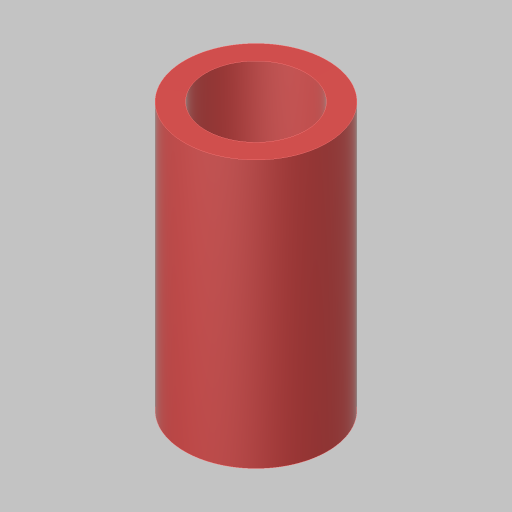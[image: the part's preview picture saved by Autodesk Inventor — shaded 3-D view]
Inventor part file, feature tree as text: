
AUTODESK INVENTOR PART (.ipt)
format: ipt  version: 2023.5 (Build 275446000, 446)  size: 101,888 bytes
history: native  units: in
note: dims shown in document units (in); Inventor stores cm internally (conversion verified against a paired STEP export)
features: extrude x1, sketch x1
ambient origin geometry x8: Origin, YZ Plane, XZ Plane, XY Plane, X Axis, Y Axis, Z Axis, Center Point
bodies: Solid1 (feature_tree)
feature tree (2):
  extrude  "Extrusion1"  Depth=1.555in
  sketch  "Sketch1"  dims[d0=0.58in d1=0.125in d2=1.555in d3=0.0in]
